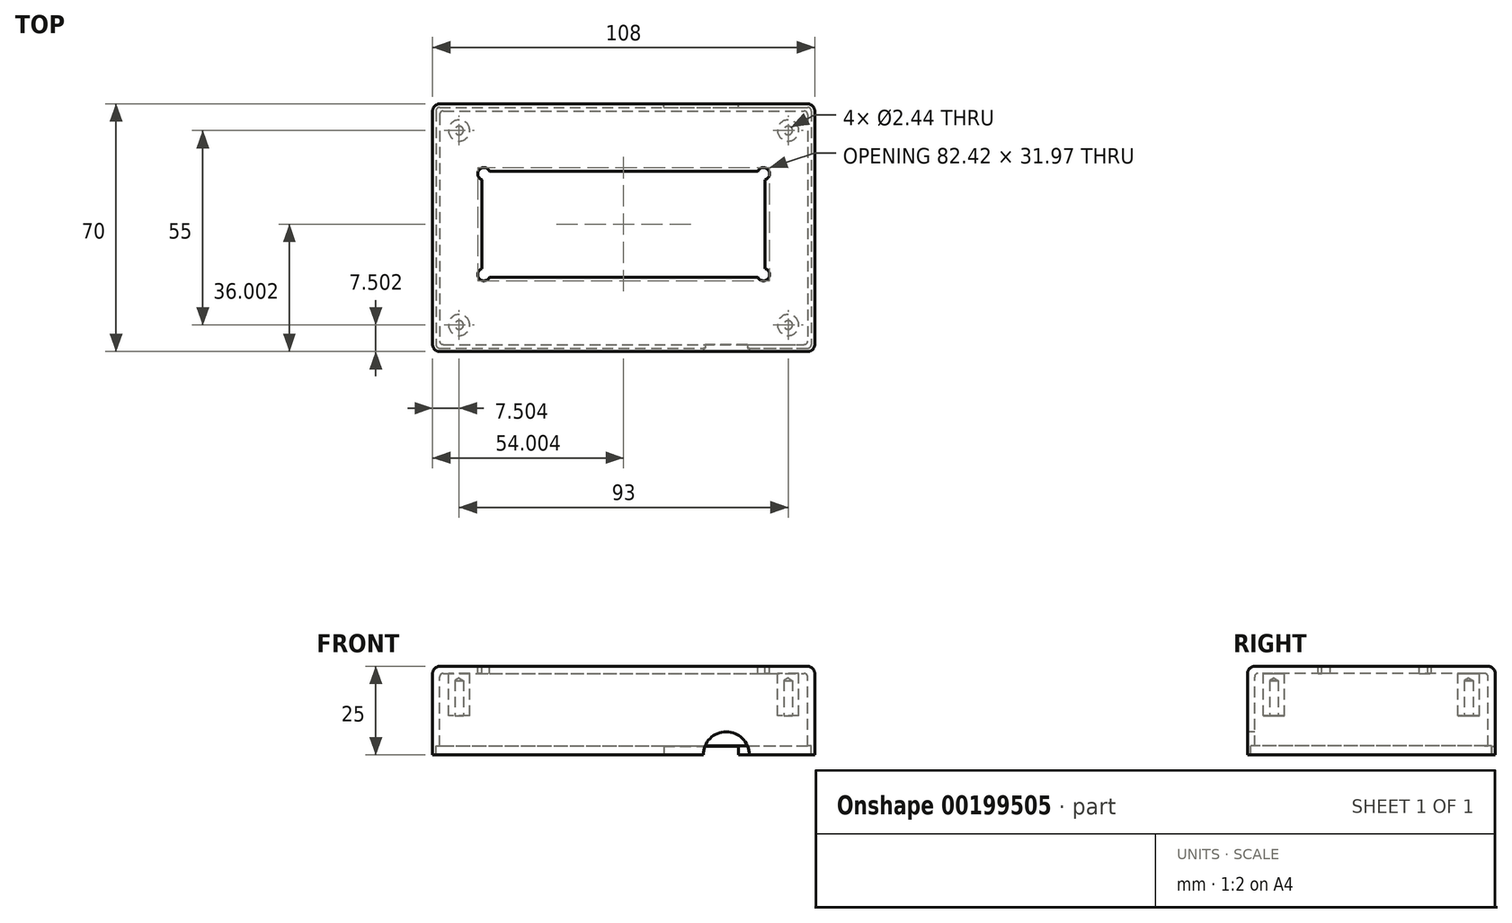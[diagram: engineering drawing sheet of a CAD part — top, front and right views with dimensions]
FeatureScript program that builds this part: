
annotation { "Feature Type Name" : "Feature", "Feature Type Description" : "" }
export const myFeature = defineFeature(function(context is Context, id is Id, definition is map)
    precondition{}
    {
        {
            var Q0;
            Q0=qCreatedBy(makeId("Top.planeOp"),FACE);
            var sketch = newSketch(context, id + "F0", { "sketchPlane" : qUnion([Q0])});
            skLineSegment(sketch, "E0.bottom", {"start": v(-55.6, 34.9) * mm, "end": v(48.4, 34.9) * mm});
            skLineSegment(sketch, "E0.top", {"start": v(-55.6, -35.1) * mm, "end": v(48.4, -35.1) * mm});
            skLineSegment(sketch, "E0.left", {"start": v(-57.6, 32.9) * mm, "end": v(-57.6, -33.1) * mm});
            skLineSegment(sketch, "E0.right", {"start": v(50.4, 32.9) * mm, "end": v(50.4, -33.1) * mm});
            skCircle(sketch, "E1", {"center": v(-43.1, 15.14) * mm, "radius": 1.75 * mm});
            skCircle(sketch, "E2", {"center": v(-43.1, -13.36) * mm, "radius": 1.75 * mm});
            skCircle(sketch, "E3", {"center": v(35.9, -13.36) * mm, "radius": 1.75 * mm});
            skCircle(sketch, "E4", {"center": v(35.9, 15.14) * mm, "radius": 1.75 * mm});
            skLineSegment(sketch, "E5.bottom", {"start": v(-55.6, 32.9) * mm, "end": v(48.4, 32.9) * mm});
            skLineSegment(sketch, "E5.top", {"start": v(-55.6, -33.1) * mm, "end": v(48.4, -33.1) * mm});
            skLineSegment(sketch, "E5.left", {"start": v(-55.6, 32.9) * mm, "end": v(-55.6, -33.1) * mm});
            skLineSegment(sketch, "E5.right", {"start": v(48.4, 32.9) * mm, "end": v(48.4, -33.1) * mm});
            skCircle(sketch, "E6", {"center": v(-50.1, 27.4) * mm, "radius": 3 * mm});
            skCircle(sketch, "E7", {"center": v(42.9, 27.4) * mm, "radius": 3 * mm});
            skCircle(sketch, "E8", {"center": v(-50.1, -27.6) * mm, "radius": 3 * mm});
            skCircle(sketch, "E9", {"center": v(42.9, -27.6) * mm, "radius": 3 * mm});
            skPoint(sketch, "E10.visualSharp", {"position": v(-55.6, -33.1) * mm});
            skPoint(sketch, "E11.visualSharp", {"position": v(-55.6, 32.9) * mm});
            skPoint(sketch, "E12.visualSharp", {"position": v(48.4, 32.9) * mm});
            skPoint(sketch, "E13.visualSharp", {"position": v(48.4, -33.1) * mm});
            skPoint(sketch, "E14.visualSharp", {"position": v(-57.6, 34.9) * mm});
            skPoint(sketch, "E15.visualSharp", {"position": v(50.4, 34.9) * mm});
            skPoint(sketch, "E16.visualSharp", {"position": v(50.4, -35.1) * mm});
            skLineSegment(sketch, "E17.bottom", {"start": v(-55.6, 33.94) * mm, "end": v(48.4, 33.94) * mm});
            skLineSegment(sketch, "E17.top", {"start": v(-55.6, -34.16) * mm, "end": v(48.4, -34.16) * mm});
            skLineSegment(sketch, "E17.left", {"start": v(-56.65, 32.9) * mm, "end": v(-56.65, -33.1) * mm});
            skLineSegment(sketch, "E17.right", {"start": v(49.45, 32.9) * mm, "end": v(49.45, -33.1) * mm});
            skLineSegment(sketch, "E18.bottom", {"start": v(-43.6, 15.9) * mm, "end": v(36.4, 15.9) * mm});
            skLineSegment(sketch, "E18.top", {"start": v(-43.6, -14.1) * mm, "end": v(36.4, -14.1) * mm});
            skLineSegment(sketch, "E18.left", {"start": v(-43.6, 15.9) * mm, "end": v(-43.6, -14.1) * mm});
            skLineSegment(sketch, "E18.right", {"start": v(36.4, 15.9) * mm, "end": v(36.4, -14.1) * mm});
            skArc(sketch, "E19.filletArc", {"start": v(-55.6, 34.9) * mm, "mid": v(-57, 34.3) * mm, "end": v(-57.6, 32.9) * mm});
            skArc(sketch, "E20.filletArc", {"start": v(50.4, 32.9) * mm, "mid": v(49.82, 34.3) * mm, "end": v(48.4, 34.9) * mm});
            skArc(sketch, "E21.filletArc", {"start": v(48.4, -35.1) * mm, "mid": v(49.82, -34.52) * mm, "end": v(50.4, -33.1) * mm});
            skPoint(sketch, "E22.visualSharp", {"position": v(-57.6, -35.1) * mm});
            skArc(sketch, "E22.filletArc", {"start": v(-57.6, -33.1) * mm, "mid": v(-57, -34.52) * mm, "end": v(-55.6, -35.1) * mm});
            skPoint(sketch, "E23.visualSharp", {"position": v(-56.65, -34.16) * mm});
            skArc(sketch, "E23.filletArc", {"start": v(-56.65, -33.1) * mm, "mid": v(-56.34, -33.85) * mm, "end": v(-55.6, -34.16) * mm});
            skPoint(sketch, "E24.visualSharp", {"position": v(49.45, -34.16) * mm});
            skArc(sketch, "E24.filletArc", {"start": v(48.4, -34.16) * mm, "mid": v(49.15, -33.85) * mm, "end": v(49.45, -33.1) * mm});
            skPoint(sketch, "E25.visualSharp", {"position": v(49.45, 33.94) * mm});
            skArc(sketch, "E25.filletArc", {"start": v(49.45, 32.9) * mm, "mid": v(49.15, 33.63) * mm, "end": v(48.4, 33.94) * mm});
            skPoint(sketch, "E26.visualSharp", {"position": v(-56.65, 33.94) * mm});
            skArc(sketch, "E26.filletArc", {"start": v(-55.6, 33.94) * mm, "mid": v(-56.34, 33.63) * mm, "end": v(-56.65, 32.9) * mm});
            skSolve(sketch);
        }
        {
            var Q0;
            Q0=makeQuery(id+"F0.imprint","IMPRINT",FACE,{"disambiguationData":[TD([[makeQuery(id+"F0.imprint","IMPRINT",EDGE,{"derivedFrom":sQuery(id+"F0.wireOp",EDGE,"E5.bottom")}),1.0]])]});
            var Q1;
            Q1=makeQuery(id+"F0.imprint","IMPRINT",FACE,{"disambiguationData":[TD([[makeQuery(id+"F0.imprint","IMPRINT",EDGE,{"derivedFrom":sQuery(id+"F0.wireOp",EDGE,"E5.bottom")}),-1.0]])]});
            var Q2;
            Q2=makeQuery(id+"F0.imprint","IMPRINT",FACE,{"disambiguationData":[TD([[makeQuery(id+"F0.imprint","IMPRINT",EDGE,{"derivedFrom":sQuery(id+"F0.wireOp",EDGE,"E6")}),1.0]])]});
            var Q3;
            Q3=makeQuery(id+"F0.imprint","IMPRINT",FACE,{"disambiguationData":[TD([[makeQuery(id+"F0.imprint","IMPRINT",EDGE,{"derivedFrom":sQuery(id+"F0.wireOp",EDGE,"E7")}),1.0]])]});
            var Q4;
            Q4=makeQuery(id+"F0.imprint","IMPRINT",FACE,{"disambiguationData":[TD([[makeQuery(id+"F0.imprint","IMPRINT",EDGE,{"derivedFrom":sQuery(id+"F0.wireOp",EDGE,"E9")}),1.0]])]});
            var Q5;
            Q5=makeQuery(id+"F0.imprint","IMPRINT",FACE,{"disambiguationData":[TD([[makeQuery(id+"F0.imprint","IMPRINT",EDGE,{"derivedFrom":sQuery(id+"F0.wireOp",EDGE,"E8")}),1.0]])]});
            var Q6;
            Q6=makeQuery(id+"F0.imprint","IMPRINT",FACE,{"disambiguationData":[TD([[makeQuery(id+"F0.imprint","IMPRINT",EDGE,{"derivedFrom":sQuery(id+"F0.wireOp",EDGE,"E0.bottom")}),-1.0]])]});
            extrude(context, id + "F1", {"entities" : qUnion([Q0, Q1, Q2, Q3, Q4, Q5, Q6]), "oppositeDirection" : true, "depth" : 2 * mm});
        }
        {
            var Q0;
            Q0=makeQuery(id+"F0.imprint","IMPRINT",FACE,{"disambiguationData":[TD([[makeQuery(id+"F0.imprint","IMPRINT",EDGE,{"derivedFrom":sQuery(id+"F0.wireOp",EDGE,"E5.bottom")}),1.0]])]});
            extrude(context, id + "F2", {"entities" : qUnion([Q0]), "operationType" : NewBodyOperationType.ADD, "oppositeDirection" : true, "depth" : 22.49 * mm});
        }
        {
            var Q0;
            {var subQ0=sQuery(id+"F0.wireOp",EDGE,"E0.right");var subQ1=sQuery(id+"F0.wireOp",EDGE,"E0.left");var subQ2=sQuery(id+"F0.wireOp",EDGE,"E0.top");var subQ3=sQuery(id+"F0.wireOp",EDGE,"E0.bottom");Q0=makeQuery(id+"F2.boolean.opBoolean","SPLIT",FACE,{"disambiguationData":[TD([makeQuery(id+"F1.opExtrude","SWEPT_FACE",FACE,{"disambiguationData":[OSD([subQ3])]})])],"derivedFrom":makeQuery(id+"F1.opExtrude","CAP_FACE",FACE,{"disambiguationData":[OSD([subQ3,subQ2,subQ1,subQ0,sQuery(id+"F0.wireOp",EDGE,"GkgKN4X4-4t61-OEX7-k9zT-44ioRnZ2twka.bottom"),sQuery(id+"F0.wireOp",EDGE,"GkgKN4X4-4t61-OEX7-k9zT-44ioRnZ2twka.top"),sQuery(id+"F0.wireOp",EDGE,"GkgKN4X4-4t61-OEX7-k9zT-44ioRnZ2twka.left"),sQuery(id+"F0.wireOp",EDGE,"GkgKN4X4-4t61-OEX7-k9zT-44ioRnZ2twka.right"),sQuery(id+"F0.wireOp",EDGE,"E1"),sQuery(id+"F0.wireOp",EDGE,"E2"),sQuery(id+"F0.wireOp",EDGE,"E3"),sQuery(id+"F0.wireOp",EDGE,"E4")])],"isStart":false})});}
            extrude(context, id + "F3", {"entities" : qUnion([Q0]), "operationType" : NewBodyOperationType.ADD, "depth" : 23 * mm});
        }
        {
            var Q0;
            Q0=makeQuery(id+"F0.imprint","IMPRINT",FACE,{"disambiguationData":[TD([[makeQuery(id+"F0.imprint","IMPRINT",EDGE,{"derivedFrom":sQuery(id+"F0.wireOp",EDGE,"E6")}),1.0]])]});
            var Q1;
            Q1=makeQuery(id+"F0.imprint","IMPRINT",FACE,{"disambiguationData":[TD([[makeQuery(id+"F0.imprint","IMPRINT",EDGE,{"derivedFrom":sQuery(id+"F0.wireOp",EDGE,"E7")}),1.0]])]});
            var Q2;
            Q2=makeQuery(id+"F0.imprint","IMPRINT",FACE,{"disambiguationData":[TD([[makeQuery(id+"F0.imprint","IMPRINT",EDGE,{"derivedFrom":sQuery(id+"F0.wireOp",EDGE,"E8")}),1.0]])]});
            var Q3;
            Q3=makeQuery(id+"F0.imprint","IMPRINT",FACE,{"disambiguationData":[TD([[makeQuery(id+"F0.imprint","IMPRINT",EDGE,{"derivedFrom":sQuery(id+"F0.wireOp",EDGE,"E9")}),1.0]])]});
            extrude(context, id + "F4", {"entities" : qUnion([Q0, Q1, Q2, Q3]), "operationType" : NewBodyOperationType.ADD, "oppositeDirection" : true, "depth" : 14 * mm});
        }
        {
            var Q0;
            {var subQ0=sQuery(id+"F0.wireOp",EDGE,"E0.top");Q0=makeQuery(id+"F3.boolean.opBoolean","MERGE",FACE,{"derivedFrom":[makeQuery(id+"F1.opExtrude","SWEPT_FACE",FACE,{"disambiguationData":[OSD([subQ0])]}),makeQuery(id+"F3.opExtrude","SWEPT_FACE",FACE,{"disambiguationData":[OSD([subQ0])]})]});}
            var sketch = newSketch(context, id + "F5", { "sketchPlane" : qUnion([Q0])});
            skPoint(sketch, "E27", {"position": v(25.4, -25) * mm});
            skCircle(sketch, "E28", {"center": v(25.4, -25) * mm, "radius": 6.5 * mm});
            skSolve(sketch);
        }
        {
            var Q0;
            {var subQ0=sQuery(id+"F5.wireOp",EDGE,"E28");var subQ1=makeQuery(id+"F3.opExtrude","CAP_EDGE",EDGE,{"disambiguationData":[OSD([sQuery(id+"F0.wireOp",EDGE,"E0.top")])],"isStart":false});var subQ2=makeQuery(id+"F5.imprint","INTERSECT",VERTEX,{"disambiguationData":[OD(0.0)],"derivedFrom":[subQ1,subQ0]});Q0=makeQuery(id+"F5.imprint","IMPRINT",FACE,{"disambiguationData":[TD([[makeQuery(id+"F5.imprint","IMPRINT",EDGE,{"disambiguationData":[TD([[subQ2,1.0]])],"derivedFrom":subQ0}),1.0]])]});}
            extrude(context, id + "F6", {"entities" : qUnion([Q0]), "operationType" : NewBodyOperationType.REMOVE, "oppositeDirection" : true, "depth" : 2.5 * mm});
        }
        {
            var Q0;
            {var subQ0=sQuery(id+"F0.wireOp",EDGE,"E0.bottom");Q0=makeQuery(id+"F3.boolean.opBoolean","MERGE",FACE,{"derivedFrom":[makeQuery(id+"F1.opExtrude","SWEPT_FACE",FACE,{"disambiguationData":[OSD([subQ0])]}),makeQuery(id+"F3.opExtrude","SWEPT_FACE",FACE,{"disambiguationData":[OSD([subQ0])]})]});}
            var sketch = newSketch(context, id + "F7", { "sketchPlane" : qUnion([Q0])});
            skLineSegment(sketch, "E29.bottom", {"start": v(-28.8, -25) * mm, "end": v(-7.8, -25) * mm});
            skLineSegment(sketch, "E29.top", {"start": v(-28.8, -22.6) * mm, "end": v(-7.8, -22.6) * mm});
            skLineSegment(sketch, "E29.left", {"start": v(-28.8, -25) * mm, "end": v(-28.8, -22.6) * mm});
            skLineSegment(sketch, "E29.right", {"start": v(-7.8, -25) * mm, "end": v(-7.8, -22.6) * mm});
            skSolve(sketch);
        }
        {
            var Q0;
            Q0=makeQuery(id+"F7.imprint","IMPRINT",FACE,{"disambiguationData":[TD([[makeQuery(id+"F7.imprint","IMPRINT",EDGE,{"derivedFrom":sQuery(id+"F7.wireOp",EDGE,"E29.bottom")}),-1.0]])]});
            extrude(context, id + "F8", {"entities" : qUnion([Q0]), "operationType" : NewBodyOperationType.REMOVE, "oppositeDirection" : true, "depth" : 2.5 * mm});
        }
        {
            var Q0;
            Q0=makeQuery(id+"F4.opExtrude","CAP_FACE",FACE,{"disambiguationData":[OSD([sQuery(id+"F0.wireOp",EDGE,"E9")])],"isStart":false});
            var sketch = newSketch(context, id + "F9", { "sketchPlane" : qUnion([Q0])});
            skPoint(sketch, "E30", {"position": v(-50.1, -27.4) * mm});
            skPoint(sketch, "E31", {"position": v(42.9, -27.4) * mm});
            skPoint(sketch, "E32", {"position": v(42.9, 27.6) * mm});
            skPoint(sketch, "E33", {"position": v(-50.1, 27.6) * mm});
            skSolve(sketch);
        }
        {
            var Q0;
            Q0=sQuery(id+"F9.wireOp",VERTEX,"E30");
            var Q1;
            Q1=sQuery(id+"F9.wireOp",VERTEX,"E31");
            var Q2;
            Q2=sQuery(id+"F9.wireOp",VERTEX,"E32");
            var Q3;
            Q3=sQuery(id+"F9.wireOp",VERTEX,"E33");
            var Q4;
            Q4=makeQuery(id+"F1.opExtrude","SWEPT_BODY",BODY,{"disambiguationData":[OSD([sQuery(id+"F0.wireOp",EDGE,"E0.bottom"),sQuery(id+"F0.wireOp",EDGE,"E0.top"),sQuery(id+"F0.wireOp",EDGE,"E0.left"),sQuery(id+"F0.wireOp",EDGE,"E0.right"),sQuery(id+"F0.wireOp",EDGE,"GkgKN4X4-4t61-OEX7-k9zT-44ioRnZ2twka.bottom"),sQuery(id+"F0.wireOp",EDGE,"GkgKN4X4-4t61-OEX7-k9zT-44ioRnZ2twka.top"),sQuery(id+"F0.wireOp",EDGE,"GkgKN4X4-4t61-OEX7-k9zT-44ioRnZ2twka.left"),sQuery(id+"F0.wireOp",EDGE,"GkgKN4X4-4t61-OEX7-k9zT-44ioRnZ2twka.right"),sQuery(id+"F0.wireOp",EDGE,"E1"),sQuery(id+"F0.wireOp",EDGE,"E2"),sQuery(id+"F0.wireOp",EDGE,"E3"),sQuery(id+"F0.wireOp",EDGE,"E4")])]});
            hole(context, id + "F10", {"style" : HoleStyle.SIMPLE, "endStyle" : HoleEndStyle.BLIND, "standardTappedOrClearance" : lookupTablePath({ "standard" : "ANSI", "size" : "#41 (0.1)", "type" : "Drilled" }), "standardBlindInLast" : lookupTablePath({ "standard" : "ANSI", "size" : "#41", "type" : "Drilled" }), "holeDiameter" : 2.44 * mm, "holeDepth" : 10 * mm, "tappedDepth" : 12 * mm, "tapClearance" : 3, "startFromSketch" : true, "locations" : qUnion([Q0, Q1, Q2, Q3]), "scope" : qUnion([Q4])});
        }
        {
            var Q0;
            Q0=makeQuery(id+"F1.opExtrude","CAP_EDGE",EDGE,{"disambiguationData":[OSD([sQuery(id+"F0.wireOp",EDGE,"E0.left")])],"isStart":true});
            var Q1;
            Q1=makeQuery(id+"F1.opExtrude","CAP_EDGE",EDGE,{"disambiguationData":[OSD([sQuery(id+"F0.wireOp",EDGE,"E0.bottom")])],"isStart":true});
            var Q2;
            Q2=makeQuery(id+"F1.opExtrude","CAP_EDGE",EDGE,{"disambiguationData":[OSD([sQuery(id+"F0.wireOp",EDGE,"E0.right")])],"isStart":true});
            var Q3;
            {var subQ0=sQuery(id+"F0.wireOp",EDGE,"E0.right");var subQ1=sQuery(id+"F0.wireOp",EDGE,"E0.top");Q3=makeQuery(id+"F3.boolean.opBoolean","MERGE",EDGE,{"derivedFrom":[makeQuery(id+"F1.opExtrude","SWEPT_EDGE",EDGE,{"disambiguationData":[OSD([subQ1,subQ0])]}),makeQuery(id+"F3.opExtrude","SWEPT_EDGE",EDGE,{"disambiguationData":[OSD([subQ1,subQ0])]})]});}
            var Q4;
            Q4=makeQuery(id+"F1.opExtrude","CAP_EDGE",EDGE,{"disambiguationData":[OSD([sQuery(id+"F0.wireOp",EDGE,"E0.top")])],"isStart":true});
            var Q5;
            {var subQ0=sQuery(id+"F0.wireOp",EDGE,"E0.left");var subQ1=sQuery(id+"F0.wireOp",EDGE,"E0.top");Q5=makeQuery(id+"F3.boolean.opBoolean","MERGE",EDGE,{"derivedFrom":[makeQuery(id+"F1.opExtrude","SWEPT_EDGE",EDGE,{"disambiguationData":[OSD([subQ1,subQ0])]}),makeQuery(id+"F3.opExtrude","SWEPT_EDGE",EDGE,{"disambiguationData":[OSD([subQ1,subQ0])]})]});}
            var Q6;
            {var subQ0=sQuery(id+"F0.wireOp",EDGE,"E0.right");var subQ1=sQuery(id+"F0.wireOp",EDGE,"E0.bottom");Q6=makeQuery(id+"F3.boolean.opBoolean","MERGE",EDGE,{"derivedFrom":[makeQuery(id+"F1.opExtrude","SWEPT_EDGE",EDGE,{"disambiguationData":[OSD([subQ1,subQ0])]}),makeQuery(id+"F3.opExtrude","SWEPT_EDGE",EDGE,{"disambiguationData":[OSD([subQ1,subQ0])]})]});}
            var Q7;
            {var subQ0=sQuery(id+"F0.wireOp",EDGE,"E0.left");var subQ1=sQuery(id+"F0.wireOp",EDGE,"E0.bottom");Q7=makeQuery(id+"F3.boolean.opBoolean","MERGE",EDGE,{"derivedFrom":[makeQuery(id+"F1.opExtrude","SWEPT_EDGE",EDGE,{"disambiguationData":[OSD([subQ1,subQ0])]}),makeQuery(id+"F3.opExtrude","SWEPT_EDGE",EDGE,{"disambiguationData":[OSD([subQ1,subQ0])]})]});}
            fillet(context, id + "F11", {"entities" : qUnion([Q0, Q1, Q2, Q3, Q4, Q5, Q6, Q7]), "radius" : 2 * mm, "tangentPropagation" : true, "allowEdgeOverflow" : false});
        }
        {
            var Q0;
            Q0=makeQuery(id+"F2.opExtrude","SWEPT_EDGE",EDGE,{"disambiguationData":[OSD([sQuery(id+"F0.wireOp",EDGE,"E5.top"),sQuery(id+"F0.wireOp",EDGE,"E5.right")])]});
            var Q1;
            Q1=makeQuery(id+"F2.boolean.opBoolean","INTERSECT",EDGE,{"derivedFrom":[makeQuery(id+"F1.opExtrude","CAP_FACE",FACE,{"disambiguationData":[OSD([sQuery(id+"F0.wireOp",EDGE,"E0.bottom"),sQuery(id+"F0.wireOp",EDGE,"E0.top"),sQuery(id+"F0.wireOp",EDGE,"E0.left"),sQuery(id+"F0.wireOp",EDGE,"E0.right"),sQuery(id+"F0.wireOp",EDGE,"GkgKN4X4-4t61-OEX7-k9zT-44ioRnZ2twka.bottom"),sQuery(id+"F0.wireOp",EDGE,"GkgKN4X4-4t61-OEX7-k9zT-44ioRnZ2twka.top"),sQuery(id+"F0.wireOp",EDGE,"GkgKN4X4-4t61-OEX7-k9zT-44ioRnZ2twka.left"),sQuery(id+"F0.wireOp",EDGE,"GkgKN4X4-4t61-OEX7-k9zT-44ioRnZ2twka.right"),sQuery(id+"F0.wireOp",EDGE,"E1"),sQuery(id+"F0.wireOp",EDGE,"E2"),sQuery(id+"F0.wireOp",EDGE,"E3"),sQuery(id+"F0.wireOp",EDGE,"E4")])],"isStart":false}),makeQuery(id+"F2.opExtrude","SWEPT_FACE",FACE,{"disambiguationData":[OSD([sQuery(id+"F0.wireOp",EDGE,"E5.right")])]})]});
            var Q2;
            Q2=makeQuery(id+"F2.boolean.opBoolean","INTERSECT",EDGE,{"derivedFrom":[makeQuery(id+"F1.opExtrude","CAP_FACE",FACE,{"disambiguationData":[OSD([sQuery(id+"F0.wireOp",EDGE,"E0.bottom"),sQuery(id+"F0.wireOp",EDGE,"E0.top"),sQuery(id+"F0.wireOp",EDGE,"E0.left"),sQuery(id+"F0.wireOp",EDGE,"E0.right"),sQuery(id+"F0.wireOp",EDGE,"GkgKN4X4-4t61-OEX7-k9zT-44ioRnZ2twka.bottom"),sQuery(id+"F0.wireOp",EDGE,"GkgKN4X4-4t61-OEX7-k9zT-44ioRnZ2twka.top"),sQuery(id+"F0.wireOp",EDGE,"GkgKN4X4-4t61-OEX7-k9zT-44ioRnZ2twka.left"),sQuery(id+"F0.wireOp",EDGE,"GkgKN4X4-4t61-OEX7-k9zT-44ioRnZ2twka.right"),sQuery(id+"F0.wireOp",EDGE,"E1"),sQuery(id+"F0.wireOp",EDGE,"E2"),sQuery(id+"F0.wireOp",EDGE,"E3"),sQuery(id+"F0.wireOp",EDGE,"E4")])],"isStart":false}),makeQuery(id+"F2.opExtrude","SWEPT_FACE",FACE,{"disambiguationData":[OSD([sQuery(id+"F0.wireOp",EDGE,"E5.top")])]})]});
            var Q3;
            Q3=makeQuery(id+"F2.opExtrude","SWEPT_EDGE",EDGE,{"disambiguationData":[OSD([sQuery(id+"F0.wireOp",EDGE,"E5.top"),sQuery(id+"F0.wireOp",EDGE,"E5.left")])]});
            var Q4;
            Q4=makeQuery(id+"F2.boolean.opBoolean","INTERSECT",EDGE,{"derivedFrom":[makeQuery(id+"F1.opExtrude","CAP_FACE",FACE,{"disambiguationData":[OSD([sQuery(id+"F0.wireOp",EDGE,"E0.bottom"),sQuery(id+"F0.wireOp",EDGE,"E0.top"),sQuery(id+"F0.wireOp",EDGE,"E0.left"),sQuery(id+"F0.wireOp",EDGE,"E0.right"),sQuery(id+"F0.wireOp",EDGE,"GkgKN4X4-4t61-OEX7-k9zT-44ioRnZ2twka.bottom"),sQuery(id+"F0.wireOp",EDGE,"GkgKN4X4-4t61-OEX7-k9zT-44ioRnZ2twka.top"),sQuery(id+"F0.wireOp",EDGE,"GkgKN4X4-4t61-OEX7-k9zT-44ioRnZ2twka.left"),sQuery(id+"F0.wireOp",EDGE,"GkgKN4X4-4t61-OEX7-k9zT-44ioRnZ2twka.right"),sQuery(id+"F0.wireOp",EDGE,"E1"),sQuery(id+"F0.wireOp",EDGE,"E2"),sQuery(id+"F0.wireOp",EDGE,"E3"),sQuery(id+"F0.wireOp",EDGE,"E4")])],"isStart":false}),makeQuery(id+"F2.opExtrude","SWEPT_FACE",FACE,{"disambiguationData":[OSD([sQuery(id+"F0.wireOp",EDGE,"E5.left")])]})]});
            var Q5;
            Q5=makeQuery(id+"F2.opExtrude","SWEPT_EDGE",EDGE,{"disambiguationData":[OSD([sQuery(id+"F0.wireOp",EDGE,"E5.bottom"),sQuery(id+"F0.wireOp",EDGE,"E5.left")])]});
            var Q6;
            Q6=makeQuery(id+"F2.boolean.opBoolean","INTERSECT",EDGE,{"derivedFrom":[makeQuery(id+"F1.opExtrude","CAP_FACE",FACE,{"disambiguationData":[OSD([sQuery(id+"F0.wireOp",EDGE,"E0.bottom"),sQuery(id+"F0.wireOp",EDGE,"E0.top"),sQuery(id+"F0.wireOp",EDGE,"E0.left"),sQuery(id+"F0.wireOp",EDGE,"E0.right"),sQuery(id+"F0.wireOp",EDGE,"GkgKN4X4-4t61-OEX7-k9zT-44ioRnZ2twka.bottom"),sQuery(id+"F0.wireOp",EDGE,"GkgKN4X4-4t61-OEX7-k9zT-44ioRnZ2twka.top"),sQuery(id+"F0.wireOp",EDGE,"GkgKN4X4-4t61-OEX7-k9zT-44ioRnZ2twka.left"),sQuery(id+"F0.wireOp",EDGE,"GkgKN4X4-4t61-OEX7-k9zT-44ioRnZ2twka.right"),sQuery(id+"F0.wireOp",EDGE,"E1"),sQuery(id+"F0.wireOp",EDGE,"E2"),sQuery(id+"F0.wireOp",EDGE,"E3"),sQuery(id+"F0.wireOp",EDGE,"E4")])],"isStart":false}),makeQuery(id+"F2.opExtrude","SWEPT_FACE",FACE,{"disambiguationData":[OSD([sQuery(id+"F0.wireOp",EDGE,"E5.bottom")])]})]});
            var Q7;
            Q7=makeQuery(id+"F2.opExtrude","SWEPT_EDGE",EDGE,{"disambiguationData":[OSD([sQuery(id+"F0.wireOp",EDGE,"E5.bottom"),sQuery(id+"F0.wireOp",EDGE,"E5.right")])]});
            fillet(context, id + "F12", {"entities" : qUnion([Q0, Q1, Q2, Q3, Q4, Q5, Q6, Q7]), "radius" : 1 * mm, "tangentPropagation" : true, "allowEdgeOverflow" : false});
        }
    });
